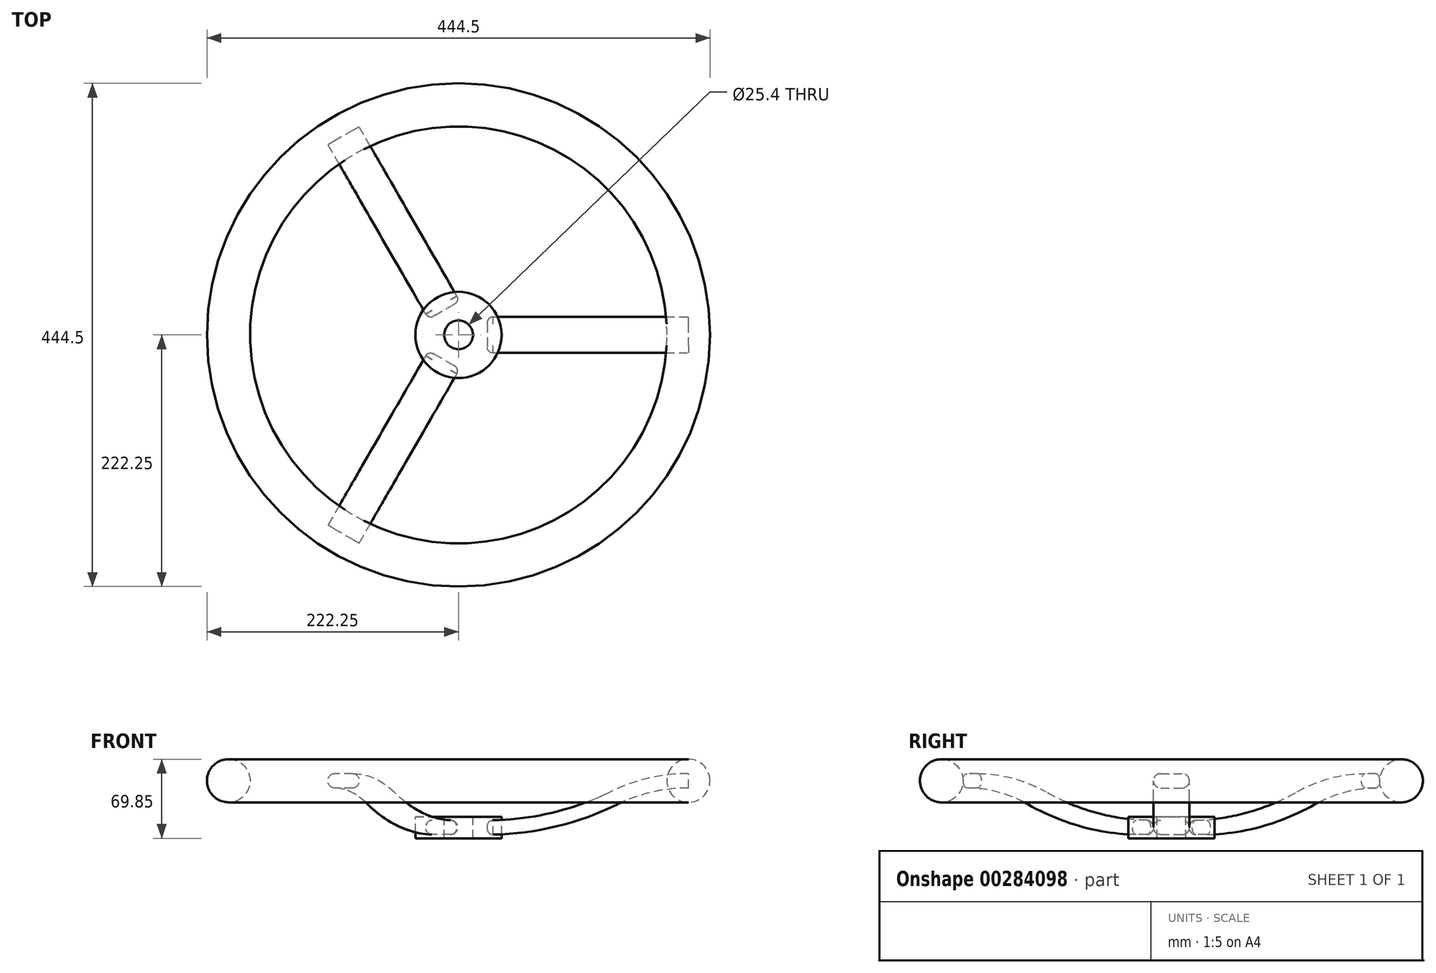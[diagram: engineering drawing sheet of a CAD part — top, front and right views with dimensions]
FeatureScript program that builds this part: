
annotation { "Feature Type Name" : "Feature", "Feature Type Description" : "" }
export const myFeature = defineFeature(function(context is Context, id is Id, definition is map)
    precondition{}
    {
        {
            var Q0;
            Q0=qCreatedBy(makeId("Front.planeOp"),FACE);
            var sketch = newSketch(context, id + "F0", { "sketchPlane" : qUnion([Q0])});
            skLineSegment(sketch, "E0.bottom", {"start": v(0, 0) * mm, "end": v(203.2, 0) * mm, "construction": true});
            skLineSegment(sketch, "E0.top", {"start": v(0, -50.8) * mm, "end": v(203.2, -50.8) * mm, "construction": true});
            skLineSegment(sketch, "E0.left", {"start": v(0, 0) * mm, "end": v(0, -50.8) * mm, "construction": true});
            skLineSegment(sketch, "E0.right", {"start": v(203.2, 0) * mm, "end": v(203.2, -50.8) * mm, "construction": true});
            skCircle(sketch, "E1", {"center": v(203.2, 0) * mm, "radius": 19.05 * mm});
            skLineSegment(sketch, "E2.bottom", {"start": v(38.1, -50.8) * mm, "end": v(12.7, -50.8) * mm});
            skLineSegment(sketch, "E2.top", {"start": v(38.1, -31.75) * mm, "end": v(12.7, -31.75) * mm});
            skLineSegment(sketch, "E2.left", {"start": v(38.1, -50.8) * mm, "end": v(38.1, -31.75) * mm});
            skLineSegment(sketch, "E2.right", {"start": v(12.7, -50.8) * mm, "end": v(12.7, -31.75) * mm});
            skPoint(sketch, "E2.middle", {"position": v(25.4, -41.27) * mm});
            skLineSegment(sketch, "E3", {"start": v(25.4, -41.27) * mm, "end": v(95.6, -41.27) * mm, "construction": true});
            skArc(sketch, "E4", {"start": v(25.4, -41.27) * mm, "mid": v(82.84, -34.7) * mm, "end": v(137.3, -15.3) * mm});
            skArc(sketch, "E5", {"start": v(203.2, 0) * mm, "mid": v(169.37, -3.87) * mm, "end": v(137.3, -15.3) * mm});
            skSolve(sketch);
        }
        {
            var Q0;
            Q0=sQuery(id+"F0.wireOp",VERTEX,"E1.center");
            var Q1;
            Q1=sQuery(id+"F0.wireOp",EDGE,"E0.bottom");
            cPlane(context, id + "F1", {"entities" : qUnion([Q0, Q1]), "cplaneType" : CPlaneType.LINE_POINT, "offset" : 25.4 * mm, "width" : 152.4 * mm, "height" : 152.4 * mm});
        }
        {
            var Q0;
            Q0=qCreatedBy(id+"F1.planeOp",FACE);
            var sketch = newSketch(context, id + "F2", { "sketchPlane" : qUnion([Q0])});
            skLineSegment(sketch, "E6.bottom", {"start": v(-9.53, -6.35) * mm, "end": v(9.52, -6.35) * mm});
            skLineSegment(sketch, "E6.top", {"start": v(-9.53, 6.35) * mm, "end": v(9.53, 6.35) * mm});
            skLineSegment(sketch, "E6.left", {"start": v(-15.88, 0) * mm, "end": v(-15.88, 0) * mm});
            skLineSegment(sketch, "E6.right", {"start": v(15.88, 0) * mm, "end": v(15.88, 0) * mm});
            skPoint(sketch, "E6.middle", {"position": v(0, 0) * mm});
            skPoint(sketch, "E7.visualSharp", {"position": v(15.88, 6.35) * mm});
            skArc(sketch, "E7.filletArc", {"start": v(15.88, 0) * mm, "mid": v(14.02, 4.5) * mm, "end": v(9.53, 6.35) * mm});
            skPoint(sketch, "E8.visualSharp", {"position": v(15.88, -6.35) * mm});
            skArc(sketch, "E8.filletArc", {"start": v(9.52, -6.35) * mm, "mid": v(14.02, -4.5) * mm, "end": v(15.87, 0) * mm});
            skPoint(sketch, "E9.visualSharp", {"position": v(-15.88, 6.35) * mm});
            skArc(sketch, "E9.filletArc", {"start": v(-9.53, 6.35) * mm, "mid": v(-14.02, 4.5) * mm, "end": v(-15.88, 0) * mm});
            skPoint(sketch, "E10.visualSharp", {"position": v(-15.88, -6.35) * mm});
            skArc(sketch, "E10.filletArc", {"start": v(-15.88, 0) * mm, "mid": v(-14.02, -4.5) * mm, "end": v(-9.53, -6.35) * mm});
            skSolve(sketch);
        }
        {
            var Q0;
            Q0=makeQuery(id+"F0.imprint","IMPRINT",FACE,{"disambiguationData":[TD([[makeQuery(id+"F0.imprint","IMPRINT",EDGE,{"derivedFrom":sQuery(id+"F0.wireOp",EDGE,"E1")}),1.0]])]});
            var Q1;
            {var subQ3=sQuery(id+"F0.wireOp",EDGE,"E2.bottom");Q1=makeQuery(id+"F0.imprint","IMPRINT",FACE,{"disambiguationData":[TD([[makeQuery(id+"F0.imprint","IMPRINT",EDGE,{"derivedFrom":subQ3}),-1.0]])]});}
            var Q2;
            Q2=sQuery(id+"F0.wireOp",EDGE,"E0.left");
            revolve(context, id + "F3", {"entities" : qUnion([Q0, Q1]), "axis" : qUnion([Q2]), "revolveType" : RevolveType.FULL});
        }
        {
            var Q0;
            Q0=makeQuery(id+"F2.imprint","IMPRINT",FACE,{"disambiguationData":[TD([[makeQuery(id+"F2.imprint","IMPRINT",EDGE,{"derivedFrom":sQuery(id+"F2.wireOp",EDGE,"E6.bottom")}),1.0]])]});
            var Q1;
            Q1=sQuery(id+"F0.wireOp",EDGE,"E5");
            var Q2;
            Q2=sQuery(id+"F0.wireOp",EDGE,"E4");
            sweep(context, id + "F4", {"profiles" : qUnion([Q0]), "path" : qUnion([Q1, Q2])});
        }
        {
            var Q0;
            Q0=makeQuery(id+"F4.opSweep","SWEPT_BODY",BODY,{"disambiguationData":[OSD([sQuery(id+"F0.wireOp",EDGE,"E4"),sQuery(id+"F2.wireOp",EDGE,"E6.bottom"),sQuery(id+"F2.wireOp",EDGE,"E6.top"),sQuery(id+"F2.wireOp",EDGE,"E7.filletArc"),sQuery(id+"F2.wireOp",EDGE,"E8.filletArc"),sQuery(id+"F2.wireOp",EDGE,"E9.filletArc"),sQuery(id+"F2.wireOp",EDGE,"E10.filletArc")])]});
            var Q1;
            Q1=makeQuery(id+"F3.opRevolve","SWEPT_FACE",FACE,{"disambiguationData":[OSD([sQuery(id+"F0.wireOp",EDGE,"E1")])]});
            circularPattern(context, id + "F5", {"entities" : qUnion([Q0]), "axis" : qUnion([Q1]), "angle" : 360 * degree, "instanceCount" : 3, "equalSpace" : true});
        }
        {
            var Q0;
            Q0=makeQuery(id+"F5.opPattern","COPY",FACE,{"derivedFrom":makeQuery(id+"F4.opSweep","SWEPT_FACE",FACE,{"disambiguationData":[OSD([sQuery(id+"F0.wireOp",EDGE,"E4"),sQuery(id+"F2.wireOp",EDGE,"E6.top")])]}),"instanceName":"2"});
            var Q1;
            Q1=makeQuery(id+"F5.opPattern","COPY",FACE,{"derivedFrom":makeQuery(id+"F4.opSweep","SWEPT_FACE",FACE,{"disambiguationData":[OSD([sQuery(id+"F0.wireOp",EDGE,"E4"),sQuery(id+"F2.wireOp",EDGE,"E6.top")])]}),"instanceName":"1"});
            var Q2;
            Q2=makeQuery(id+"F4.opSweep","SWEPT_FACE",FACE,{"disambiguationData":[OSD([sQuery(id+"F0.wireOp",EDGE,"E4"),sQuery(id+"F2.wireOp",EDGE,"E6.top")])]});
            var Q3;
            Q3=makeQuery(id+"F3.opRevolve","SWEPT_FACE",FACE,{"disambiguationData":[OSD([sQuery(id+"F0.wireOp",EDGE,"E1")])]});
            fillet(context, id + "F6", {"entities" : qUnion([Q0, Q1, Q2, Q3]), "radius" : 5.08 * mm, "tangentPropagation" : true, "allowEdgeOverflow" : false});
        }
    });
